# Revit family: LAMP_FIL 35 CORNER OPAL RECESSED HC
name_source: partatom
category: Luminarias
revit_build: Autodesk Revit 2018 (Build: 20190510_1515(x64)
units: mm (PartAtom-declared; Revit-internal decimal feet)

## family parameters
Anfitrión = Cara
Compartido = No
Corte con vacíos al cargar = No
Cota de conector redondo = Diámetro de uso
Origen de luz = Sí
Punto de cálculo de habitación = No
Tipo de pieza = Normal

## types (12) — shared parameters
Archivo de red fotométrica = F31SF084LOOP830NB.IES
CRI = 80
Cambio de temperatura de color de luz atenuada = <Ninguno>
Dimensions = 313x313x35
Efficacy = 95 lm/W
Elevación por defecto = 1219 mm
Fabricante = LAMP
Filtro de color = 16777215
Gear = Electronic
IEE = A+
Installation instructions = https://www.lamp.es
Insulation class = I
LED Lifetime = 60.000 L80 B10
Lamp = MID-POWER LED
Last update = 24/05/2021
MacAdam = 3
Manufacturer URL = http://www.lamp.es
Manufacturer country = Spain
Manufacturer name = LAMP
Material difusor = LAMP_PC Difusor Opal Fil
Material suspension = LAMP_Acero genérico
Plum = 6 W
Power = 5 W
Power Supply = 220-240V 50/60Hz
Product URL = https://www.lamp.es
Product datasheet = http://www.lamp.es
Protection rating = IP20 / IK07
Recessed dimensions = 319x319x42
Type = MID POWER TRIDONIC
Weight = 1.23 kg
Ángulo de inclinación = -90.00°

## per-type parameters (varying)
| type | Descripción | Finish | Material perfil | Modelo | Product code | Second light |
| 577LM 3000K DALI BLACK | FIL35 HORIZ. CORNER REC 800 WW OPAL DA B | Matte black RAL 9011 | LAMP_Aluminio Perfil Fil NG | F31REHCLOOP830DB | F31REHCLOOP830DB | LAMP_FIL 35 CORNER OPAL SURFACE HC_SECOND : 3000K |
| 577LM 3000K DALI GREY | FIL35 HORIZ. CORNER REC 800 WW OPAL DA G | Gloss grey | LAMP_Aluminio Perfil Fil GR | F31REHCLOOP830DG | F31REHCLOOP830DG | LAMP_FIL 35 CORNER OPAL SURFACE HC_SECOND : 3000K |
| 577LM 3000K DALI WHITE | FIL35 HORIZ. CORNER REC 800 WW OPAL DA W | Matte white RAL 9010 | LAMP_Aluminio Perfil Fil BL | F31REHCLOOP830DW | F31REHCLOOP830DW | LAMP_FIL 35 CORNER OPAL SURFACE HC_SECOND : 3000K |
| 577LM 3000K  BLACK | FIL35 HORIZ. CORNER REC 800 WW OPAL BK. | Matte black RAL 9011 | LAMP_Aluminio Perfil Fil NG | F31REHCLOOP830NB | F31REHCLOOP830NB | LAMP_FIL 35 CORNER OPAL SURFACE HC_SECOND : 3000K |
| 577LM 3000K  GREY | FIL35 HORIZ. CORNER REC 800 WW OPAL GR. | Gloss grey | LAMP_Aluminio Perfil Fil GR | F31REHCLOOP830NG | F31REHCLOOP830NG | LAMP_FIL 35 CORNER OPAL SURFACE HC_SECOND : 3000K |
| 577LM 3000K  WHITE | FIL35 HORIZ. CORNER REC 800 WW OPAL WH. | Matte white RAL 9010 | LAMP_Aluminio Perfil Fil BL | F31REHCLOOP830NW | F31REHCLOOP830NW | LAMP_FIL 35 CORNER OPAL SURFACE HC_SECOND : 3000K |
| 577LM 4000K DALI BLACK | FIL35 HORIZ. CORNER REC 800 NW OPAL DA B | Matte black RAL 9011 | LAMP_Aluminio Perfil Fil NG | F31REHCLOOP840DB | F31REHCLOOP840DB | LAMP_FIL 35 CORNER OPAL SURFACE HC_SECOND : 4000K |
| 577LM 4000K DALI GREY | FIL35 HORIZ. CORNER REC 800 NW OPAL DA G | Gloss grey | LAMP_Aluminio Perfil Fil GR | F31REHCLOOP840DG | F31REHCLOOP840DG | LAMP_FIL 35 CORNER OPAL SURFACE HC_SECOND : 4000K |
| 577LM 4000K DALI WHITE | FIL35 HORIZ. CORNER REC 800 NW OPAL DA W | Matte white RAL 9010 | LAMP_Aluminio Perfil Fil BL | F31REHCLOOP840DW | F31REHCLOOP840DW | LAMP_FIL 35 CORNER OPAL SURFACE HC_SECOND : 4000K |
| 577LM 4000K  BLACK | FIL35 HORIZ. CORNER REC 800 NW OPAL BK. | Matte black RAL 9011 | LAMP_Aluminio Perfil Fil NG | F31REHCLOOP840NB | F31REHCLOOP840NB | LAMP_FIL 35 CORNER OPAL SURFACE HC_SECOND : 4000K |
| 577LM 4000K  GREY | FIL35 HORIZ. CORNER REC 800 NW OPAL GR. | Gloss grey | LAMP_Aluminio Perfil Fil GR | F31REHCLOOP840NG | F31REHCLOOP840NG | LAMP_FIL 35 CORNER OPAL SURFACE HC_SECOND : 4000K |
| 577LM 4000K  WHITE | FIL35 HORIZ. CORNER REC 800 NW OPAL WH. | Matte white RAL 9010 | LAMP_Aluminio Perfil Fil BL | F31REHCLOOP840NW | F31REHCLOOP840NW | LAMP_FIL 35 CORNER OPAL SURFACE HC_SECOND : 4000K |
